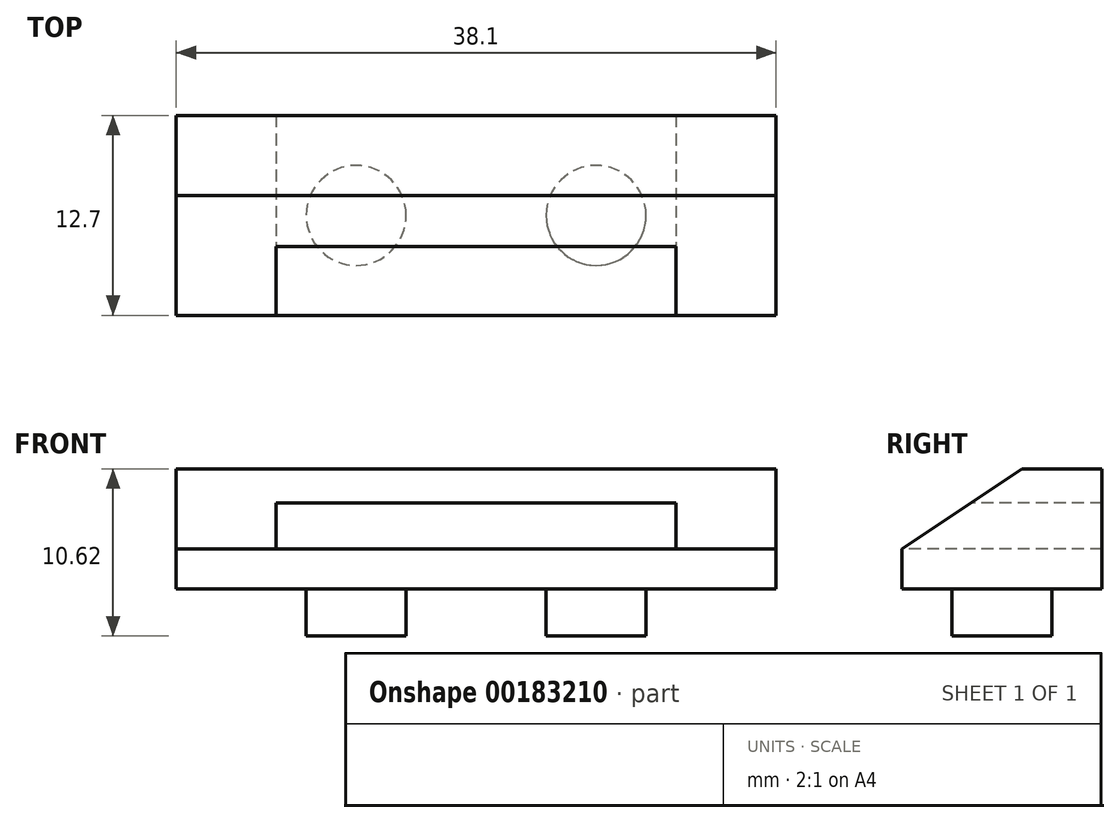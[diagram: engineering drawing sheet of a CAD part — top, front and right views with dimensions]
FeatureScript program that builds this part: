
annotation { "Feature Type Name" : "Feature", "Feature Type Description" : "" }
export const myFeature = defineFeature(function(context is Context, id is Id, definition is map)
    precondition{}
    {
        {
            var Q0;
            Q0=qCreatedBy(makeId("Top.planeOp"),FACE);
            var sketch = newSketch(context, id + "F0", { "sketchPlane" : qUnion([Q0])});
            skLineSegment(sketch, "E0.bottom", {"start": v(0, 0) * mm, "end": v(38.1, 0) * mm});
            skLineSegment(sketch, "E0.top", {"start": v(0, 12.7) * mm, "end": v(38.1, 12.7) * mm});
            skLineSegment(sketch, "E0.left", {"start": v(0, 0) * mm, "end": v(0, 12.7) * mm});
            skLineSegment(sketch, "E0.right", {"start": v(38.1, 0) * mm, "end": v(38.1, 12.7) * mm});
            skSolve(sketch);
        }
        {
            var Q0;
            Q0=makeQuery(id+"F0.imprint","IMPRINT",FACE,{"disambiguationData":[TD([[makeQuery(id+"F0.imprint","IMPRINT",EDGE,{"derivedFrom":sQuery(id+"F0.wireOp",EDGE,"E0.bottom")}),1.0]])]});
            extrude(context, id + "F1", {"entities" : qUnion([Q0]), "depth" : 2.54 * mm});
        }
        {
            var Q0;
            Q0=makeQuery(id+"F1.opExtrude","SWEPT_FACE",FACE,{"disambiguationData":[OSD([sQuery(id+"F0.wireOp",EDGE,"E0.right")])]});
            var sketch = newSketch(context, id + "F2", { "sketchPlane" : qUnion([Q0])});
            skLineSegment(sketch, "E1", {"start": v(12.7, 2.54) * mm, "end": v(12.7, 7.62) * mm});
            skLineSegment(sketch, "E2", {"start": v(12.7, 7.62) * mm, "end": v(7.62, 7.62) * mm});
            skLineSegment(sketch, "E3", {"start": v(7.62, 7.62) * mm, "end": v(0, 2.54) * mm});
            skLineSegment(sketch, "E4", {"start": v(0, 2.54) * mm, "end": v(12.7, 2.54) * mm});
            skSolve(sketch);
        }
        {
            var Q0;
            Q0=makeQuery(id+"F2.imprint","IMPRINT",FACE,{"disambiguationData":[TD([[makeQuery(id+"F2.imprint","IMPRINT",EDGE,{"derivedFrom":sQuery(id+"F2.wireOp",EDGE,"E1")}),1.0]])]});
            extrude(context, id + "F3", {"entities" : qUnion([Q0]), "operationType" : NewBodyOperationType.ADD, "oppositeDirection" : true, "depth" : 38.1 * mm});
        }
        {
            var Q0;
            Q0=makeQuery(id+"F1.opExtrude","SWEPT_FACE",FACE,{"disambiguationData":[OSD([sQuery(id+"F0.wireOp",EDGE,"E0.bottom")])]});
            var sketch = newSketch(context, id + "F4", { "sketchPlane" : qUnion([Q0])});
            skLineSegment(sketch, "E5", {"start": v(0, 2.54) * mm, "end": v(6.35, 2.54) * mm, "construction": true});
            skLineSegment(sketch, "E6", {"start": v(6.35, 2.54) * mm, "end": v(0, 2.54) * mm, "construction": true});
            skLineSegment(sketch, "E7", {"start": v(38.1, 2.54) * mm, "end": v(31.75, 2.54) * mm, "construction": true});
            skLineSegment(sketch, "E8", {"start": v(31.75, 2.54) * mm, "end": v(38.1, 2.54) * mm, "construction": true});
            skLineSegment(sketch, "E9", {"start": v(38.1, 2.54) * mm, "end": v(38.1, 5.46) * mm, "construction": true});
            skLineSegment(sketch, "E10", {"start": v(38.1, 5.46) * mm, "end": v(0, 5.46) * mm, "construction": true});
            skLineSegment(sketch, "E11.bottom", {"start": v(6.35, 2.54) * mm, "end": v(31.75, 2.54) * mm});
            skLineSegment(sketch, "E11.top", {"start": v(6.35, 5.46) * mm, "end": v(31.75, 5.46) * mm});
            skLineSegment(sketch, "E11.left", {"start": v(6.35, 2.54) * mm, "end": v(6.35, 5.46) * mm});
            skLineSegment(sketch, "E11.right", {"start": v(31.75, 2.54) * mm, "end": v(31.75, 5.46) * mm});
            skSolve(sketch);
        }
        {
            var Q0;
            Q0=makeQuery(id+"F4.imprint","IMPRINT",FACE,{"disambiguationData":[TD([[makeQuery(id+"F4.imprint","IMPRINT",EDGE,{"derivedFrom":sQuery(id+"F4.wireOp",EDGE,"E11.bottom")}),1.0]])]});
            extrude(context, id + "F5", {"entities" : qUnion([Q0]), "operationType" : NewBodyOperationType.REMOVE, "oppositeDirection" : true, "depth" : 12.7 * mm});
        }
        {
            var Q0;
            Q0=makeQuery(id+"F1.opExtrude","CAP_FACE",FACE,{"disambiguationData":[OSD([sQuery(id+"F0.wireOp",EDGE,"E0.bottom"),sQuery(id+"F0.wireOp",EDGE,"E0.top"),sQuery(id+"F0.wireOp",EDGE,"E0.left"),sQuery(id+"F0.wireOp",EDGE,"E0.right")])],"isStart":true});
            var sketch = newSketch(context, id + "F6", { "sketchPlane" : qUnion([Q0])});
            skLineSegment(sketch, "E12", {"start": v(0, -12.7) * mm, "end": v(38.1, -12.7) * mm, "construction": true});
            skLineSegment(sketch, "E13", {"start": v(38.1, -12.7) * mm, "end": v(19.05, -12.7) * mm, "construction": true});
            skLineSegment(sketch, "E14", {"start": v(19.05, -12.7) * mm, "end": v(19.05, 0) * mm, "construction": true});
            skLineSegment(sketch, "E15", {"start": v(19.05, 0) * mm, "end": v(19.05, -6.35) * mm, "construction": true});
            skLineSegment(sketch, "E16", {"start": v(19.05, -6.35) * mm, "end": v(26.67, -6.35) * mm, "construction": true});
            skLineSegment(sketch, "E17", {"start": v(26.67, -6.35) * mm, "end": v(11.43, -6.35) * mm, "construction": true});
            skLineSegment(sketch, "E18", {"start": v(11.43, -6.35) * mm, "end": v(26.67, -6.35) * mm, "construction": true});
            skCircle(sketch, "E19", {"center": v(11.43, -6.35) * mm, "radius": 3.18 * mm});
            skCircle(sketch, "E20", {"center": v(26.67, -6.35) * mm, "radius": 3.18 * mm});
            skSolve(sketch);
        }
        {
            var Q0;
            Q0=makeQuery(id+"F6.imprint","IMPRINT",FACE,{"disambiguationData":[TD([[makeQuery(id+"F6.imprint","IMPRINT",EDGE,{"derivedFrom":sQuery(id+"F6.wireOp",EDGE,"E19")}),1.0]])]});
            var Q1;
            Q1=makeQuery(id+"F6.imprint","IMPRINT",FACE,{"disambiguationData":[TD([[makeQuery(id+"F6.imprint","IMPRINT",EDGE,{"derivedFrom":sQuery(id+"F6.wireOp",EDGE,"E20")}),1.0]])]});
            extrude(context, id + "F7", {"entities" : qUnion([Q0, Q1]), "operationType" : NewBodyOperationType.ADD, "depth" : 3 * mm});
        }
    });
